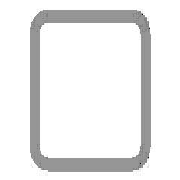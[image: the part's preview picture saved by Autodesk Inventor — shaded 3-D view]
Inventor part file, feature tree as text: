
AUTODESK INVENTOR PART (.ipt)
format: ipt  version: 2022 (Build 260153000, 153)  size: 154,624 bytes
history: native  units: mm (DEFAULTED — no unit token found)
features: other x4, plane x3, sketch x3, split x2, extrude x1
ambient origin geometry x8: Origin, YZ Plane, XZ Plane, XY Plane, X Axis, Y Axis, Z Axis, Center Point
bodies: Solid1 (feature_tree)
feature tree (13):
  parser-record x1  (decoder bookkeeping rows leaked as tree rows — omitted from the tree; the rows remain in map.json)
  other  "Driven Length"
  other  "Plano inicial"
  other  "Plano final"
  extrude  "Cuerpo"  TaperAngle=0.0deg  [1 undecoded]
  plane  "Plano de trabajo4"
  split  "Dividir1"
  plane  "Plano de trabajo5"
  split  "Dividir2"
  sketch  "Boceto"  dims[d10=40.0mm d11=40.0mm d12=5.0mm d13=-11.768067mm d14=211.095123mm d15=20.0mm d16=20.0mm d17=90.0deg d18=222.86319mm]
  sketch  "Sketch3"  dims[d3=222.86319mm d4=0.0mm]
  plane  "Work Plane3"
  sketch  "Sketch4"  dims[d7=7.5mm]
note: 1 required parameter value undecoded (feature->parameter linkage not recoverable at this tier; creation-order binding heuristic only, values carry confidence <= 0.55)
